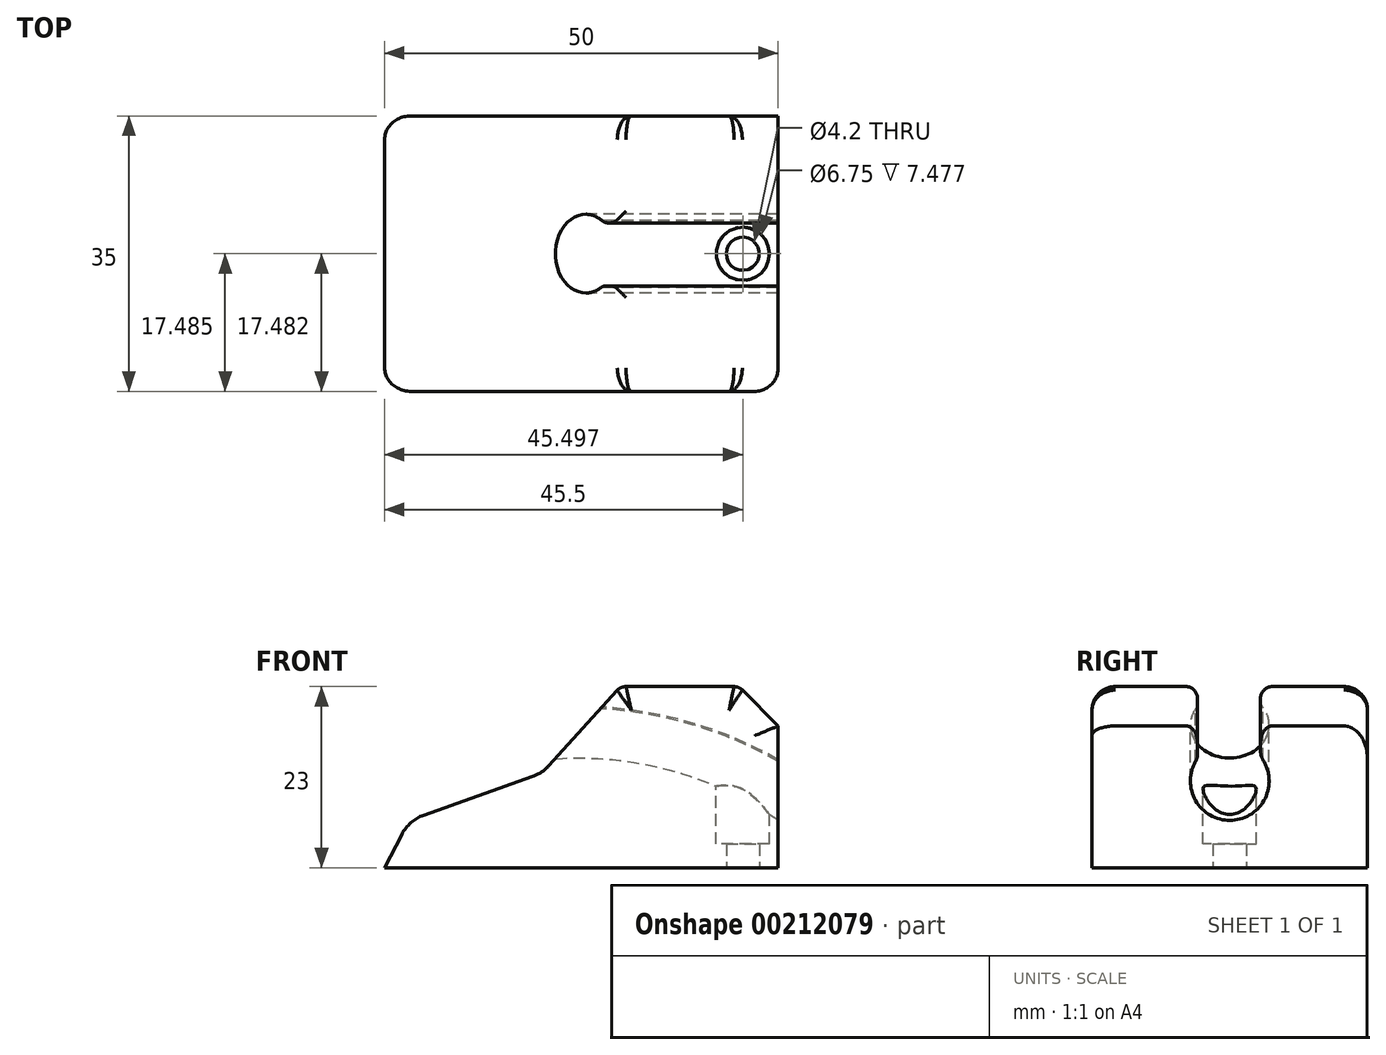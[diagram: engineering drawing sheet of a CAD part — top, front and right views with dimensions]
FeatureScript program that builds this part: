
annotation { "Feature Type Name" : "Feature", "Feature Type Description" : "" }
export const myFeature = defineFeature(function(context is Context, id is Id, definition is map)
    precondition{}
    {
        {
            var Q0;
            Q0=qCreatedBy(makeId("Front.planeOp"),FACE);
            var sketch = newSketch(context, id + "F0", { "sketchPlane" : qUnion([Q0])});
            skLineSegment(sketch, "E0", {"start": v(-50, 0) * mm, "end": v(0, 0) * mm});
            skLineSegment(sketch, "E1", {"start": v(0, 0) * mm, "end": v(0, 18) * mm});
            skLineSegment(sketch, "E2", {"start": v(0, 18) * mm, "end": v(-5, 23) * mm});
            skLineSegment(sketch, "E3", {"start": v(-5, 23) * mm, "end": v(-20, 23) * mm});
            skLineSegment(sketch, "E4", {"start": v(-20, 23) * mm, "end": v(-30, 12) * mm});
            skLineSegment(sketch, "E5", {"start": v(-30, 12) * mm, "end": v(-46.9, 6) * mm});
            skLineSegment(sketch, "E6", {"start": v(-46.9, 6) * mm, "end": v(-50, 0) * mm});
            skCircle(sketch, "E7", {"center": v(-25.4, -30.7) * mm, "radius": 45 * mm});
            skLineSegment(sketch, "E8", {"start": v(-30, 12) * mm, "end": v(-27.98, 14.22) * mm});
            skSolve(sketch);
        }
        {
            var Q0;
            Q0=makeQuery(id+"F0.imprint","IMPRINT",FACE,{"disambiguationData":[TD([[makeQuery(id+"F0.imprint","IMPRINT",EDGE,{"derivedFrom":sQuery(id+"F0.wireOp",EDGE,"E0")}),1.0]])]});
            extrude(context, id + "F1", {"entities" : qUnion([Q0]), "depth" : 35 * mm});
        }
        {
            var Q0;
            Q0=makeQuery(id+"F1.opExtrude","SWEPT_FACE",FACE,{"disambiguationData":[OSD([sQuery(id+"F0.wireOp",EDGE,"E1")])]});
            var sketch = newSketch(context, id + "F2", { "sketchPlane" : qUnion([Q0])});
            skCircle(sketch, "E9", {"center": v(-17.5, 11) * mm, "radius": 5 * mm});
            skLineSegment(sketch, "E10", {"start": v(-17.6, 25.71) * mm, "end": v(-21.6, 25.71) * mm});
            skLineSegment(sketch, "E11", {"start": v(-17.6, 25.71) * mm, "end": v(-13.6, 25.71) * mm});
            skLineSegment(sketch, "E12", {"start": v(-21.6, 25.71) * mm, "end": v(-21.6, 13.87) * mm});
            skLineSegment(sketch, "E13", {"start": v(-13.6, 25.71) * mm, "end": v(-13.6, 14.12) * mm});
            skSolve(sketch);
        }
        {
            var Q0;
            {var subQ1=sQuery(id+"F0.wireOp",EDGE,"E2");Q0=makeQuery(id+"F0.imprint","IMPRINT",FACE,{"disambiguationData":[TD([[makeQuery(id+"F0.imprint","IMPRINT",EDGE,{"derivedFrom":subQ1}),1.0]])]});}
            extrude(context, id + "F3", {"entities" : qUnion([Q0]), "operationType" : NewBodyOperationType.ADD, "depth" : 35 * mm});
        }
        {
            var Q0;
            {var subQ0=sQuery(id+"F2.wireOp",EDGE,"sB516rDa-i3NP-vVBW-9Blr-pMs61KeMCDnR");var subQ1=sQuery(id+"F2.wireOp",EDGE,"E9");var subQ2=makeQuery(id+"F2.imprint","INTERSECT",VERTEX,{"disambiguationData":[OD(0.0)],"derivedFrom":[subQ1,subQ0]});Q0=makeQuery(id+"F2.imprint","IMPRINT",FACE,{"disambiguationData":[TD([[makeQuery(id+"F2.imprint","IMPRINT",EDGE,{"disambiguationData":[TD([[subQ2,1.0]])],"derivedFrom":subQ1}),1.0]])]});}
            var Q1;
            {var subQ0=sQuery(id+"F2.wireOp",EDGE,"sB516rDa-i3NP-vVBW-9Blr-pMs61KeMCDnR");var subQ1=sQuery(id+"F2.wireOp",EDGE,"E9");var subQ2=makeQuery(id+"F2.imprint","INTERSECT",VERTEX,{"disambiguationData":[OD(0.0)],"derivedFrom":[subQ1,subQ0]});Q1=makeQuery(id+"F2.imprint","IMPRINT",FACE,{"disambiguationData":[TD([[makeQuery(id+"F2.imprint","IMPRINT",EDGE,{"disambiguationData":[TD([[subQ2,-1.0]])],"derivedFrom":subQ1}),1.0]])]});}
            var Q2;
            Q2=makeQuery(id+"F2.imprint","IMPRINT",FACE,{"disambiguationData":[TD([[makeQuery(id+"F2.imprint","IMPRINT",EDGE,{"derivedFrom":sQuery(id+"F2.wireOp",EDGE,"E10")}),1.0]])]});
            var Q3;
            Q3=sQuery(id+"F0.wireOp",EDGE,"E7");
            sweep(context, id + "F4", {"operationType" : NewBodyOperationType.REMOVE, "profiles" : qUnion([Q0, Q1, Q2]), "path" : qUnion([Q3])});
        }
        {
            var Q0;
            Q0=makeQuery(id+"F4.boolean.opBoolean","COPY",EDGE,{"derivedFrom":makeQuery(id+"F4.opSweep","SWEPT_EDGE",EDGE,{"disambiguationData":[OSD([sQuery(id+"F0.wireOp",EDGE,"E7"),sQuery(id+"F2.wireOp",EDGE,"E9"),sQuery(id+"F2.wireOp",EDGE,"ul9TaXmI-i2gY-oxA1-I6sm-kJ49Mk5RbQbl"),sQuery(id+"F2.wireOp",EDGE,"SNI9qfWH-SGdS-5PZx-1Rih-pm4xFIWWbr9O")])]})});
            var Q1;
            Q1=makeQuery(id+"F4.boolean.opBoolean","COPY",EDGE,{"derivedFrom":makeQuery(id+"F4.opSweep","SWEPT_EDGE",EDGE,{"disambiguationData":[OSD([sQuery(id+"F0.wireOp",EDGE,"E7"),sQuery(id+"F2.wireOp",EDGE,"E9"),sQuery(id+"F2.wireOp",EDGE,"t4GUBAWO-RxcE-c0CZ-GoJe-D8SvXsJvo8gx")])]})});
            var Q2;
            Q2=makeQuery(id+"F4.boolean.opBoolean","INTERSECT",EDGE,{"derivedFrom":[makeQuery(id+"F3.opExtrude","SWEPT_FACE",FACE,{"disambiguationData":[OSD([sQuery(id+"F0.wireOp",EDGE,"E2")])]}),makeQuery(id+"F4.opSweep","SWEPT_FACE",FACE,{"disambiguationData":[OSD([sQuery(id+"F0.wireOp",EDGE,"E7"),sQuery(id+"F2.wireOp",EDGE,"ul9TaXmI-i2gY-oxA1-I6sm-kJ49Mk5RbQbl")])]})]});
            var Q3;
            Q3=makeQuery(id+"F4.boolean.opBoolean","INTERSECT",EDGE,{"derivedFrom":[makeQuery(id+"F3.opExtrude","SWEPT_FACE",FACE,{"disambiguationData":[OSD([sQuery(id+"F0.wireOp",EDGE,"E3")])]}),makeQuery(id+"F4.opSweep","SWEPT_FACE",FACE,{"disambiguationData":[OSD([sQuery(id+"F0.wireOp",EDGE,"E7"),sQuery(id+"F2.wireOp",EDGE,"ul9TaXmI-i2gY-oxA1-I6sm-kJ49Mk5RbQbl")])]})]});
            var Q4;
            Q4=makeQuery(id+"F4.boolean.opBoolean","INTERSECT",EDGE,{"derivedFrom":[makeQuery(id+"F3.opExtrude","SWEPT_FACE",FACE,{"disambiguationData":[OSD([sQuery(id+"F0.wireOp",EDGE,"E2")])]}),makeQuery(id+"F4.opSweep","SWEPT_FACE",FACE,{"disambiguationData":[OSD([sQuery(id+"F0.wireOp",EDGE,"E7"),sQuery(id+"F2.wireOp",EDGE,"t4GUBAWO-RxcE-c0CZ-GoJe-D8SvXsJvo8gx")])]})]});
            var Q5;
            Q5=makeQuery(id+"F4.boolean.opBoolean","INTERSECT",EDGE,{"derivedFrom":[makeQuery(id+"F3.opExtrude","SWEPT_FACE",FACE,{"disambiguationData":[OSD([sQuery(id+"F0.wireOp",EDGE,"E3")])]}),makeQuery(id+"F4.opSweep","SWEPT_FACE",FACE,{"disambiguationData":[OSD([sQuery(id+"F0.wireOp",EDGE,"E7"),sQuery(id+"F2.wireOp",EDGE,"t4GUBAWO-RxcE-c0CZ-GoJe-D8SvXsJvo8gx")])]})]});
            var Q6;
            {var subQ0=sQuery(id+"F0.wireOp",EDGE,"E3");var subQ2=sQuery(id+"F0.wireOp",EDGE,"E7");var subQ3=sQuery(id+"F0.wireOp",EDGE,"E4");Q6=makeQuery(id+"F4.boolean.opBoolean","SPLIT",EDGE,{"disambiguationData":[TD([makeQuery(id+"F4.opSweep","SWEPT_FACE",FACE,{"disambiguationData":[OSD([subQ2,sQuery(id+"F2.wireOp",EDGE,"ul9TaXmI-i2gY-oxA1-I6sm-kJ49Mk5RbQbl")])]})])],"derivedFrom":makeQuery(id+"F3.opExtrude","SWEPT_EDGE",EDGE,{"disambiguationData":[OSD([subQ0,subQ3])]})});}
            var Q7;
            {var subQ0=sQuery(id+"F0.wireOp",EDGE,"E3");var subQ1=sQuery(id+"F0.wireOp",EDGE,"E7");var subQ2=sQuery(id+"F0.wireOp",EDGE,"E4");Q7=makeQuery(id+"F4.boolean.opBoolean","SPLIT",EDGE,{"disambiguationData":[TD([makeQuery(id+"F4.opSweep","SWEPT_FACE",FACE,{"disambiguationData":[OSD([subQ1,sQuery(id+"F2.wireOp",EDGE,"t4GUBAWO-RxcE-c0CZ-GoJe-D8SvXsJvo8gx")])]})])],"derivedFrom":makeQuery(id+"F3.opExtrude","SWEPT_EDGE",EDGE,{"disambiguationData":[OSD([subQ0,subQ2])]})});}
            var Q8;
            {var subQ0=sQuery(id+"F0.wireOp",EDGE,"E3");var subQ1=sQuery(id+"F0.wireOp",EDGE,"E2");var subQ2=sQuery(id+"F0.wireOp",EDGE,"E7");Q8=makeQuery(id+"F4.boolean.opBoolean","SPLIT",EDGE,{"disambiguationData":[TD([makeQuery(id+"F4.opSweep","SWEPT_FACE",FACE,{"disambiguationData":[OSD([subQ2,sQuery(id+"F2.wireOp",EDGE,"ul9TaXmI-i2gY-oxA1-I6sm-kJ49Mk5RbQbl")])]})])],"derivedFrom":makeQuery(id+"F3.opExtrude","SWEPT_EDGE",EDGE,{"disambiguationData":[OSD([subQ1,subQ0])]})});}
            var Q9;
            {var subQ0=sQuery(id+"F0.wireOp",EDGE,"E3");var subQ1=sQuery(id+"F0.wireOp",EDGE,"E2");var subQ2=sQuery(id+"F0.wireOp",EDGE,"E7");Q9=makeQuery(id+"F4.boolean.opBoolean","SPLIT",EDGE,{"disambiguationData":[TD([makeQuery(id+"F4.opSweep","SWEPT_FACE",FACE,{"disambiguationData":[OSD([subQ2,sQuery(id+"F2.wireOp",EDGE,"t4GUBAWO-RxcE-c0CZ-GoJe-D8SvXsJvo8gx")])]})])],"derivedFrom":makeQuery(id+"F3.opExtrude","SWEPT_EDGE",EDGE,{"disambiguationData":[OSD([subQ1,subQ0])]})});}
            fillet(context, id + "F5", {"entities" : qUnion([Q0, Q1, Q2, Q3, Q4, Q5, Q6, Q7, Q8, Q9]), "radius" : 1.5 * mm, "tangentPropagation" : true, "allowEdgeOverflow" : false});
        }
        {
            var Q0;
            Q0=makeQuery(id+"F1.opExtrude","SWEPT_EDGE",EDGE,{"disambiguationData":[OSD([sQuery(id+"F0.wireOp",EDGE,"E5"),sQuery(id+"F0.wireOp",EDGE,"E6")])]});
            var Q1;
            Q1=makeQuery(id+"F1.opExtrude","SWEPT_EDGE",EDGE,{"disambiguationData":[OSD([sQuery(id+"F0.wireOp",EDGE,"E5"),sQuery(id+"F0.wireOp",EDGE,"E8")])]});
            fillet(context, id + "F6", {"entities" : qUnion([Q0, Q1]), "radius" : 5 * mm, "tangentPropagation" : true, "allowEdgeOverflow" : false});
        }
        {
            var Q0;
            Q0=makeQuery(id+"F1.opExtrude","CAP_EDGE",EDGE,{"disambiguationData":[OSD([sQuery(id+"F0.wireOp",EDGE,"E6")])],"isStart":false});
            var Q1;
            {var subQ0=sQuery(id+"F0.wireOp",EDGE,"E7");var subQ1=sQuery(id+"F0.wireOp",EDGE,"E1");var subQ2=sQuery(id+"F0.wireOp",EDGE,"E6");var subQ3=sQuery(id+"F0.wireOp",EDGE,"E5");Q1=makeQuery(id+"F6.opFillet","BLEND_EDGE",EDGE,{"blendedFrom":[makeQuery(id+"F1.opExtrude","SWEPT_EDGE",EDGE,{"disambiguationData":[OSD([subQ3,subQ2])]}),makeQuery(id+"F3.boolean.opBoolean","MERGE",FACE,{"derivedFrom":[makeQuery(id+"F1.opExtrude","CAP_FACE",FACE,{"disambiguationData":[OSD([sQuery(id+"F0.wireOp",EDGE,"E0"),subQ1,subQ3,subQ2,subQ0,sQuery(id+"F0.wireOp",EDGE,"E8")])],"isStart":false}),makeQuery(id+"F3.opExtrude","CAP_FACE",FACE,{"disambiguationData":[OSD([subQ1,sQuery(id+"F0.wireOp",EDGE,"E2"),sQuery(id+"F0.wireOp",EDGE,"E3"),sQuery(id+"F0.wireOp",EDGE,"E4"),subQ0])],"isStart":false})]})],"blendedInto":[makeQuery(id+"F3.boolean.opBoolean","MERGE",FACE,{"derivedFrom":[makeQuery(id+"F1.opExtrude","CAP_FACE",FACE,{"disambiguationData":[OSD([sQuery(id+"F0.wireOp",EDGE,"E0"),subQ1,subQ3,subQ2,subQ0,sQuery(id+"F0.wireOp",EDGE,"E8")])],"isStart":false}),makeQuery(id+"F3.opExtrude","CAP_FACE",FACE,{"disambiguationData":[OSD([subQ1,sQuery(id+"F0.wireOp",EDGE,"E2"),sQuery(id+"F0.wireOp",EDGE,"E3"),sQuery(id+"F0.wireOp",EDGE,"E4"),subQ0])],"isStart":false})]})]});}
            var Q2;
            Q2=makeQuery(id+"F1.opExtrude","CAP_EDGE",EDGE,{"disambiguationData":[OSD([sQuery(id+"F0.wireOp",EDGE,"E5")])],"isStart":false});
            var Q3;
            {var subQ0=sQuery(id+"F0.wireOp",EDGE,"E7");var subQ1=sQuery(id+"F0.wireOp",EDGE,"E1");var subQ2=sQuery(id+"F0.wireOp",EDGE,"E8");var subQ3=sQuery(id+"F0.wireOp",EDGE,"E5");Q3=makeQuery(id+"F6.opFillet","BLEND_EDGE",EDGE,{"blendedFrom":[makeQuery(id+"F1.opExtrude","SWEPT_EDGE",EDGE,{"disambiguationData":[OSD([subQ3,subQ2])]}),makeQuery(id+"F3.boolean.opBoolean","MERGE",FACE,{"derivedFrom":[makeQuery(id+"F1.opExtrude","CAP_FACE",FACE,{"disambiguationData":[OSD([sQuery(id+"F0.wireOp",EDGE,"E0"),subQ1,subQ3,sQuery(id+"F0.wireOp",EDGE,"E6"),subQ0,subQ2])],"isStart":false}),makeQuery(id+"F3.opExtrude","CAP_FACE",FACE,{"disambiguationData":[OSD([subQ1,sQuery(id+"F0.wireOp",EDGE,"E2"),sQuery(id+"F0.wireOp",EDGE,"E3"),sQuery(id+"F0.wireOp",EDGE,"E4"),subQ0])],"isStart":false})]})],"blendedInto":[makeQuery(id+"F3.boolean.opBoolean","MERGE",FACE,{"derivedFrom":[makeQuery(id+"F1.opExtrude","CAP_FACE",FACE,{"disambiguationData":[OSD([sQuery(id+"F0.wireOp",EDGE,"E0"),subQ1,subQ3,sQuery(id+"F0.wireOp",EDGE,"E6"),subQ0,subQ2])],"isStart":false}),makeQuery(id+"F3.opExtrude","CAP_FACE",FACE,{"disambiguationData":[OSD([subQ1,sQuery(id+"F0.wireOp",EDGE,"E2"),sQuery(id+"F0.wireOp",EDGE,"E3"),sQuery(id+"F0.wireOp",EDGE,"E4"),subQ0])],"isStart":false})]})]});}
            var Q4;
            Q4=makeQuery(id+"F3.boolean.opBoolean","MERGE",EDGE,{"derivedFrom":[makeQuery(id+"F1.opExtrude","CAP_EDGE",EDGE,{"disambiguationData":[OSD([sQuery(id+"F0.wireOp",EDGE,"E8")])],"isStart":false}),makeQuery(id+"F3.opExtrude","CAP_EDGE",EDGE,{"disambiguationData":[OSD([sQuery(id+"F0.wireOp",EDGE,"E4")])],"isStart":false})]});
            var Q5;
            Q5=makeQuery(id+"F3.opExtrude","CAP_EDGE",EDGE,{"disambiguationData":[OSD([sQuery(id+"F0.wireOp",EDGE,"E3")])],"isStart":false});
            var Q6;
            {var subQ0=sQuery(id+"F0.wireOp",EDGE,"E7");var subQ1=sQuery(id+"F0.wireOp",EDGE,"E4");var subQ2=sQuery(id+"F0.wireOp",EDGE,"E3");var subQ3=sQuery(id+"F0.wireOp",EDGE,"E1");var subQ4=makeQuery(id+"F3.opExtrude","CAP_FACE",FACE,{"disambiguationData":[OSD([subQ3,sQuery(id+"F0.wireOp",EDGE,"E2"),subQ2,subQ1,subQ0])],"isStart":false});var subQ5=sQuery(id+"F0.wireOp",EDGE,"E8");var subQ6=makeQuery(id+"F1.opExtrude","CAP_FACE",FACE,{"disambiguationData":[OSD([sQuery(id+"F0.wireOp",EDGE,"E0"),subQ3,sQuery(id+"F0.wireOp",EDGE,"E5"),sQuery(id+"F0.wireOp",EDGE,"E6"),subQ0,subQ5])],"isStart":false});Q6=makeQuery(id+"F5.opFillet","BLEND_EDGE",EDGE,{"blendedFrom":[makeQuery(id+"F4.boolean.opBoolean","SPLIT",EDGE,{"disambiguationData":[TD([makeQuery(id+"F4.opSweep","SWEPT_FACE",FACE,{"disambiguationData":[OSD([subQ0,sQuery(id+"F2.wireOp",EDGE,"t4GUBAWO-RxcE-c0CZ-GoJe-D8SvXsJvo8gx")])]})])],"derivedFrom":makeQuery(id+"F3.opExtrude","SWEPT_EDGE",EDGE,{"disambiguationData":[OSD([subQ2,subQ1])]})}),makeQuery(id+"F3.boolean.opBoolean","MERGE",FACE,{"derivedFrom":[subQ6,subQ4]})],"blendedInto":[makeQuery(id+"F3.boolean.opBoolean","MERGE",FACE,{"derivedFrom":[subQ6,subQ4]})]});}
            var Q7;
            {var subQ0=sQuery(id+"F0.wireOp",EDGE,"E7");var subQ1=sQuery(id+"F0.wireOp",EDGE,"E3");var subQ2=sQuery(id+"F0.wireOp",EDGE,"E2");var subQ3=sQuery(id+"F0.wireOp",EDGE,"E1");var subQ4=makeQuery(id+"F3.opExtrude","CAP_FACE",FACE,{"disambiguationData":[OSD([subQ3,subQ2,subQ1,sQuery(id+"F0.wireOp",EDGE,"E4"),subQ0])],"isStart":false});var subQ5=makeQuery(id+"F1.opExtrude","CAP_FACE",FACE,{"disambiguationData":[OSD([sQuery(id+"F0.wireOp",EDGE,"E0"),subQ3,sQuery(id+"F0.wireOp",EDGE,"E5"),sQuery(id+"F0.wireOp",EDGE,"E6"),subQ0,sQuery(id+"F0.wireOp",EDGE,"E8")])],"isStart":false});Q7=makeQuery(id+"F5.opFillet","BLEND_EDGE",EDGE,{"blendedFrom":[makeQuery(id+"F4.boolean.opBoolean","SPLIT",EDGE,{"disambiguationData":[TD([makeQuery(id+"F4.opSweep","SWEPT_FACE",FACE,{"disambiguationData":[OSD([subQ0,sQuery(id+"F2.wireOp",EDGE,"t4GUBAWO-RxcE-c0CZ-GoJe-D8SvXsJvo8gx")])]})])],"derivedFrom":makeQuery(id+"F3.opExtrude","SWEPT_EDGE",EDGE,{"disambiguationData":[OSD([subQ2,subQ1])]})}),makeQuery(id+"F3.boolean.opBoolean","MERGE",FACE,{"derivedFrom":[subQ5,subQ4]})],"blendedInto":[makeQuery(id+"F3.boolean.opBoolean","MERGE",FACE,{"derivedFrom":[subQ5,subQ4]})]});}
            var Q8;
            Q8=makeQuery(id+"F3.opExtrude","CAP_EDGE",EDGE,{"disambiguationData":[OSD([sQuery(id+"F0.wireOp",EDGE,"E2")])],"isStart":false});
            var Q9;
            {var subQ0=sQuery(id+"F0.wireOp",EDGE,"E1");Q9=makeQuery(id+"F3.boolean.opBoolean","MERGE",EDGE,{"derivedFrom":[makeQuery(id+"F1.opExtrude","CAP_EDGE",EDGE,{"disambiguationData":[OSD([subQ0])],"isStart":false}),makeQuery(id+"F3.opExtrude","CAP_EDGE",EDGE,{"disambiguationData":[OSD([subQ0])],"isStart":false})]});}
            fillet(context, id + "F7", {"entities" : qUnion([Q0, Q1, Q2, Q3, Q4, Q5, Q6, Q7, Q8, Q9]), "radius" : 3 * mm, "tangentPropagation" : true, "allowEdgeOverflow" : false});
        }
        {
            var Q0;
            {var subQ0=sQuery(id+"F0.wireOp",EDGE,"E7");var subQ1=sQuery(id+"F0.wireOp",EDGE,"E1");var subQ2=sQuery(id+"F0.wireOp",EDGE,"E6");var subQ3=sQuery(id+"F0.wireOp",EDGE,"E5");Q0=makeQuery(id+"F6.opFillet","BLEND_EDGE",EDGE,{"blendedFrom":[makeQuery(id+"F1.opExtrude","SWEPT_EDGE",EDGE,{"disambiguationData":[OSD([subQ3,subQ2])]}),makeQuery(id+"F3.boolean.opBoolean","MERGE",FACE,{"derivedFrom":[makeQuery(id+"F1.opExtrude","CAP_FACE",FACE,{"disambiguationData":[OSD([sQuery(id+"F0.wireOp",EDGE,"E0"),subQ1,subQ3,subQ2,subQ0,sQuery(id+"F0.wireOp",EDGE,"E8")])],"isStart":true}),makeQuery(id+"F3.opExtrude","CAP_FACE",FACE,{"disambiguationData":[OSD([subQ1,sQuery(id+"F0.wireOp",EDGE,"E2"),sQuery(id+"F0.wireOp",EDGE,"E3"),sQuery(id+"F0.wireOp",EDGE,"E4"),subQ0])],"isStart":true})]})],"blendedInto":[makeQuery(id+"F3.boolean.opBoolean","MERGE",FACE,{"derivedFrom":[makeQuery(id+"F1.opExtrude","CAP_FACE",FACE,{"disambiguationData":[OSD([sQuery(id+"F0.wireOp",EDGE,"E0"),subQ1,subQ3,subQ2,subQ0,sQuery(id+"F0.wireOp",EDGE,"E8")])],"isStart":true}),makeQuery(id+"F3.opExtrude","CAP_FACE",FACE,{"disambiguationData":[OSD([subQ1,sQuery(id+"F0.wireOp",EDGE,"E2"),sQuery(id+"F0.wireOp",EDGE,"E3"),sQuery(id+"F0.wireOp",EDGE,"E4"),subQ0])],"isStart":true})]})]});}
            var Q1;
            {var subQ0=sQuery(id+"F0.wireOp",EDGE,"E7");var subQ1=sQuery(id+"F0.wireOp",EDGE,"E1");var subQ2=sQuery(id+"F0.wireOp",EDGE,"E8");var subQ3=sQuery(id+"F0.wireOp",EDGE,"E5");Q1=makeQuery(id+"F6.opFillet","BLEND_EDGE",EDGE,{"blendedFrom":[makeQuery(id+"F1.opExtrude","SWEPT_EDGE",EDGE,{"disambiguationData":[OSD([subQ3,subQ2])]}),makeQuery(id+"F3.boolean.opBoolean","MERGE",FACE,{"derivedFrom":[makeQuery(id+"F1.opExtrude","CAP_FACE",FACE,{"disambiguationData":[OSD([sQuery(id+"F0.wireOp",EDGE,"E0"),subQ1,subQ3,sQuery(id+"F0.wireOp",EDGE,"E6"),subQ0,subQ2])],"isStart":true}),makeQuery(id+"F3.opExtrude","CAP_FACE",FACE,{"disambiguationData":[OSD([subQ1,sQuery(id+"F0.wireOp",EDGE,"E2"),sQuery(id+"F0.wireOp",EDGE,"E3"),sQuery(id+"F0.wireOp",EDGE,"E4"),subQ0])],"isStart":true})]})],"blendedInto":[makeQuery(id+"F3.boolean.opBoolean","MERGE",FACE,{"derivedFrom":[makeQuery(id+"F1.opExtrude","CAP_FACE",FACE,{"disambiguationData":[OSD([sQuery(id+"F0.wireOp",EDGE,"E0"),subQ1,subQ3,sQuery(id+"F0.wireOp",EDGE,"E6"),subQ0,subQ2])],"isStart":true}),makeQuery(id+"F3.opExtrude","CAP_FACE",FACE,{"disambiguationData":[OSD([subQ1,sQuery(id+"F0.wireOp",EDGE,"E2"),sQuery(id+"F0.wireOp",EDGE,"E3"),sQuery(id+"F0.wireOp",EDGE,"E4"),subQ0])],"isStart":true})]})]});}
            fillet(context, id + "F8", {"entities" : qUnion([Q0, Q1]), "radius" : 3 * mm, "tangentPropagation" : true, "allowEdgeOverflow" : false});
        }
        {
            var Q0;
            Q0=makeQuery(id+"F1.opExtrude","SWEPT_FACE",FACE,{"disambiguationData":[OSD([sQuery(id+"F0.wireOp",EDGE,"E0")])]});
            var sketch = newSketch(context, id + "F9", { "sketchPlane" : qUnion([Q0])});
            skLineSegment(sketch, "E14.bottom", {"start": v(0, 22.01) * mm, "end": v(-9, 22.01) * mm});
            skLineSegment(sketch, "E14.top", {"start": v(0, 13.01) * mm, "end": v(-9, 13.01) * mm});
            skLineSegment(sketch, "E14.left", {"start": v(0, 22.01) * mm, "end": v(0, 13.01) * mm});
            skLineSegment(sketch, "E14.right", {"start": v(-9, 22.01) * mm, "end": v(-9, 13.01) * mm});
            skLineSegment(sketch, "E15", {"start": v(0, 22.01) * mm, "end": v(-9, 13.01) * mm});
            skLineSegment(sketch, "E16", {"start": v(-9, 22.01) * mm, "end": v(0, 13.01) * mm});
            skCircle(sketch, "E17", {"center": v(-4.5, 17.51) * mm, "radius": 2.1 * mm});
            skCircle(sketch, "E18", {"center": v(-4.5, 17.51) * mm, "radius": 3.38 * mm});
            skSolve(sketch);
        }
        {
            var Q0;
            {var subQ0=sQuery(id+"F9.wireOp",EDGE,"E17");var subQ1=sQuery(id+"F9.wireOp",EDGE,"E15");var subQ2=makeQuery(id+"F9.imprint","INTERSECT",VERTEX,{"disambiguationData":[OD(0.0)],"derivedFrom":[subQ1,subQ0]});Q0=makeQuery(id+"F9.imprint","IMPRINT",FACE,{"disambiguationData":[TD([[makeQuery(id+"F9.imprint","IMPRINT",EDGE,{"disambiguationData":[TD([[subQ2,-1.0]])],"derivedFrom":subQ1}),-1.0]])]});}
            var Q1;
            {var subQ0=sQuery(id+"F9.wireOp",EDGE,"E17");var subQ1=sQuery(id+"F9.wireOp",EDGE,"E15");var subQ2=makeQuery(id+"F9.imprint","INTERSECT",VERTEX,{"disambiguationData":[OD(0.0)],"derivedFrom":[subQ1,subQ0]});Q1=makeQuery(id+"F9.imprint","IMPRINT",FACE,{"disambiguationData":[TD([[makeQuery(id+"F9.imprint","IMPRINT",EDGE,{"disambiguationData":[TD([[subQ2,-1.0]])],"derivedFrom":subQ1}),1.0]])]});}
            var Q2;
            {var subQ0=sQuery(id+"F9.wireOp",EDGE,"E16");var subQ1=sQuery(id+"F9.wireOp",EDGE,"E15");var subQ2=makeQuery(id+"F9.imprint","INTERSECT",VERTEX,{"derivedFrom":[subQ1,subQ0]});Q2=makeQuery(id+"F9.imprint","IMPRINT",FACE,{"disambiguationData":[TD([[makeQuery(id+"F9.imprint","IMPRINT",EDGE,{"disambiguationData":[TD([[subQ2,-1.0]])],"derivedFrom":subQ1}),1.0]])]});}
            var Q3;
            {var subQ0=sQuery(id+"F9.wireOp",EDGE,"E16");var subQ1=sQuery(id+"F9.wireOp",EDGE,"E15");var subQ2=makeQuery(id+"F9.imprint","INTERSECT",VERTEX,{"derivedFrom":[subQ1,subQ0]});Q3=makeQuery(id+"F9.imprint","IMPRINT",FACE,{"disambiguationData":[TD([[makeQuery(id+"F9.imprint","IMPRINT",EDGE,{"disambiguationData":[TD([[subQ2,-1.0]])],"derivedFrom":subQ1}),-1.0]])]});}
            extrude(context, id + "F10", {"entities" : qUnion([Q0, Q1, Q2, Q3]), "operationType" : NewBodyOperationType.REMOVE, "oppositeDirection" : true, "depth" : 45 * mm});
        }
        {
            var Q0;
            {var subQ9=sQuery(id+"F9.wireOp",EDGE,"E14.bottom");Q0=makeQuery(id+"F9.imprint","IMPRINT",FACE,{"disambiguationData":[TD([[makeQuery(id+"F9.imprint","IMPRINT",EDGE,{"derivedFrom":subQ9}),-1.0]])]});}
            cPlane(context, id + "F11", {"entities" : qUnion([Q0]), "cplaneType" : CPlaneType.OFFSET, "offset" : 25 * mm, "oppositeDirection" : true, "width" : 150 * mm, "height" : 150 * mm});
        }
        {
            var Q0;
            Q0=qCreatedBy(id+"F11.planeOp",FACE);
            var sketch = newSketch(context, id + "F12", { "sketchPlane" : qUnion([Q0])});
            skCircle(sketch, "E19", {"center": v(-4.5, 17.52) * mm, "radius": 3.38 * mm});
            skCircle(sketch, "E20", {"center": v(-4.5, 17.52) * mm, "radius": 2.1 * mm});
            skSolve(sketch);
        }
        {
            var Q0;
            Q0=makeQuery(id+"F12.imprint","IMPRINT",FACE,{"disambiguationData":[TD([[makeQuery(id+"F12.imprint","IMPRINT",EDGE,{"derivedFrom":sQuery(id+"F12.wireOp",EDGE,"E19")}),1.0]])]});
            extrude(context, id + "F13", {"entities" : qUnion([Q0]), "operationType" : NewBodyOperationType.REMOVE, "depth" : 22 * mm});
        }
    });
